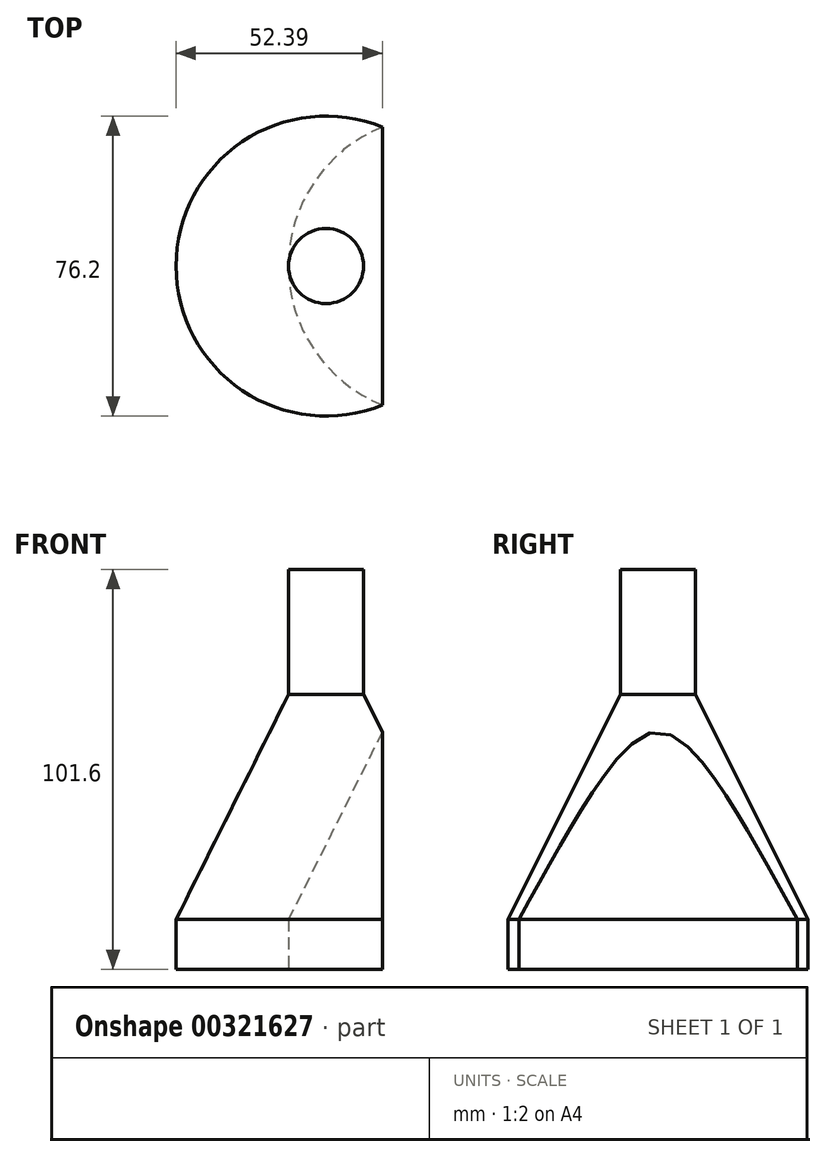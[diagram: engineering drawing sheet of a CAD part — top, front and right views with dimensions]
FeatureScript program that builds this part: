
annotation { "Feature Type Name" : "Feature", "Feature Type Description" : "" }
export const myFeature = defineFeature(function(context is Context, id is Id, definition is map)
    precondition{}
    {
        {
            var Q0;
            Q0=qCreatedBy(makeId("Front.planeOp"),FACE);
            var sketch = newSketch(context, id + "F0", { "sketchPlane" : qUnion([Q0])});
            skLineSegment(sketch, "E0", {"start": v(0, 0) * mm, "end": v(0, 31.75) * mm, "construction": true});
            skLineSegment(sketch, "E1", {"start": v(0, 31.75) * mm, "end": v(9.52, 31.75) * mm});
            skLineSegment(sketch, "E2", {"start": v(9.53, 31.75) * mm, "end": v(9.53, 0) * mm});
            skLineSegment(sketch, "E3", {"start": v(9.52, 0) * mm, "end": v(38.1, -57.15) * mm});
            skLineSegment(sketch, "E4", {"start": v(38.1, -57.15) * mm, "end": v(38.1, -69.85) * mm});
            skLineSegment(sketch, "E5", {"start": v(38.1, -69.85) * mm, "end": v(0, -69.85) * mm});
            skLineSegment(sketch, "E6", {"start": v(0, 31.75) * mm, "end": v(0, -69.85) * mm});
            skSolve(sketch);
        }
        {
            var Q0;
            Q0 = qSketchRegion(id + "F0", true);
            var Q1;
            Q1=sQuery(id+"F0.wireOp",EDGE,"E0");
            revolve(context, id + "F1", {"entities" : qUnion([Q0]), "axis" : qUnion([Q1]), "revolveType" : RevolveType.FULL});
        }
        {
            var Q0;
            Q0=makeQuery(id+"F1.opRevolve","SWEPT_BODY",BODY,{"disambiguationData":[OSD([sQuery(id+"F0.wireOp",EDGE,"E1"),sQuery(id+"F0.wireOp",EDGE,"E2"),sQuery(id+"F0.wireOp",EDGE,"E3"),sQuery(id+"F0.wireOp",EDGE,"E4"),sQuery(id+"F0.wireOp",EDGE,"E5"),sQuery(id+"F0.wireOp",EDGE,"6cffce98-ed6d-4752-95ab-70827d12d298.0"),sQuery(id+"F0.wireOp",EDGE,"6cffce98-ed6d-4752-95ab-70827d12d298.1"),sQuery(id+"F0.wireOp",EDGE,"6cffce98-ed6d-4752-95ab-70827d12d298.2"),sQuery(id+"F0.wireOp",EDGE,"6cffce98-ed6d-4752-95ab-70827d12d298.3"),sQuery(id+"F0.wireOp",EDGE,"6cffce98-ed6d-4752-95ab-70827d12d298.4"),sQuery(id+"F0.wireOp",EDGE,"LZUBdMsW-NZLa-2cMp-E1xW-asSrOQVLWIoc"),sQuery(id+"F0.wireOp",EDGE,"LHPwzYbd-iZi3-Sxs4-8aeP-KWnq5UMweIE4")])]});
            transform(context, id + "F2", {"entities" : qUnion([Q0]), "transformType" : TransformType.TRANSLATION_3D, "dx" : 28.57 * mm, "dy" : 0 * mm, "dz" : 0 * mm, "makeCopy" : true});
        }
        {
            var Q0;
            Q0=makeQuery(id+"F2.opPattern","COPY",BODY,{"derivedFrom":makeQuery(id+"F1.opRevolve","SWEPT_BODY",BODY,{"disambiguationData":[OSD([sQuery(id+"F0.wireOp",EDGE,"E1"),sQuery(id+"F0.wireOp",EDGE,"E2"),sQuery(id+"F0.wireOp",EDGE,"E3"),sQuery(id+"F0.wireOp",EDGE,"E4"),sQuery(id+"F0.wireOp",EDGE,"E5"),sQuery(id+"F0.wireOp",EDGE,"6cffce98-ed6d-4752-95ab-70827d12d298.0"),sQuery(id+"F0.wireOp",EDGE,"6cffce98-ed6d-4752-95ab-70827d12d298.1"),sQuery(id+"F0.wireOp",EDGE,"6cffce98-ed6d-4752-95ab-70827d12d298.2"),sQuery(id+"F0.wireOp",EDGE,"6cffce98-ed6d-4752-95ab-70827d12d298.3"),sQuery(id+"F0.wireOp",EDGE,"6cffce98-ed6d-4752-95ab-70827d12d298.4"),sQuery(id+"F0.wireOp",EDGE,"LZUBdMsW-NZLa-2cMp-E1xW-asSrOQVLWIoc"),sQuery(id+"F0.wireOp",EDGE,"LHPwzYbd-iZi3-Sxs4-8aeP-KWnq5UMweIE4")])]}),"instanceName":"1"});
            var Q1;
            Q1=makeQuery(id+"F1.opRevolve","SWEPT_BODY",BODY,{"disambiguationData":[OSD([sQuery(id+"F0.wireOp",EDGE,"E1"),sQuery(id+"F0.wireOp",EDGE,"E2"),sQuery(id+"F0.wireOp",EDGE,"E3"),sQuery(id+"F0.wireOp",EDGE,"E4"),sQuery(id+"F0.wireOp",EDGE,"E5"),sQuery(id+"F0.wireOp",EDGE,"6cffce98-ed6d-4752-95ab-70827d12d298.0"),sQuery(id+"F0.wireOp",EDGE,"6cffce98-ed6d-4752-95ab-70827d12d298.1"),sQuery(id+"F0.wireOp",EDGE,"6cffce98-ed6d-4752-95ab-70827d12d298.2"),sQuery(id+"F0.wireOp",EDGE,"6cffce98-ed6d-4752-95ab-70827d12d298.3"),sQuery(id+"F0.wireOp",EDGE,"6cffce98-ed6d-4752-95ab-70827d12d298.4"),sQuery(id+"F0.wireOp",EDGE,"LZUBdMsW-NZLa-2cMp-E1xW-asSrOQVLWIoc"),sQuery(id+"F0.wireOp",EDGE,"LHPwzYbd-iZi3-Sxs4-8aeP-KWnq5UMweIE4")])]});
            booleanBodies(context, id + "F3", {"operationType" : BooleanOperationType.SUBTRACTION, "tools" : qUnion([Q0]), "targets" : qUnion([Q1])});
        }
    });
